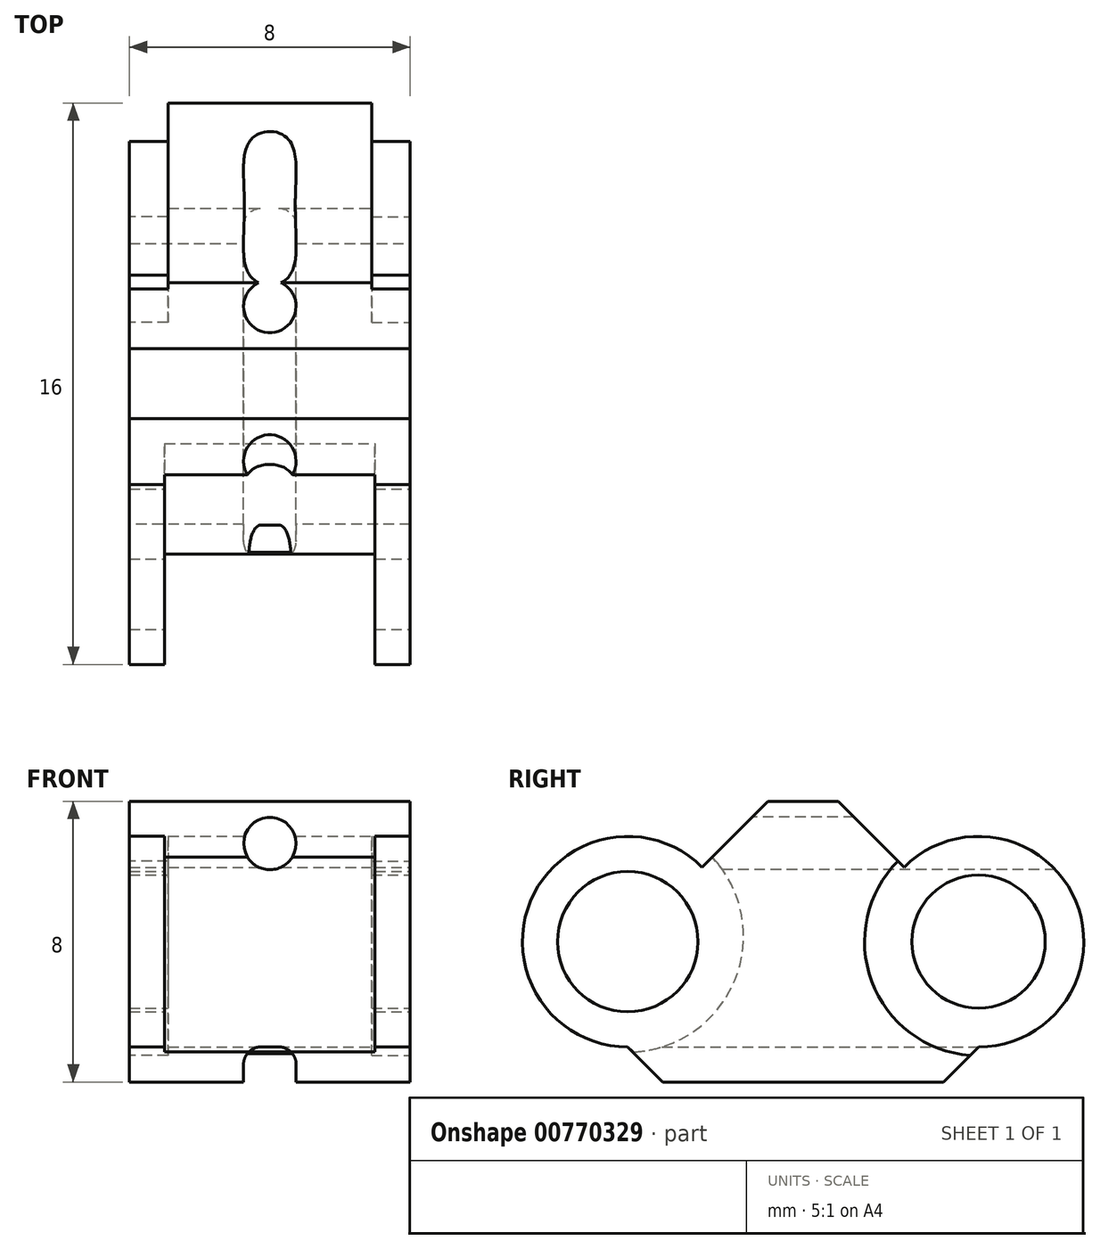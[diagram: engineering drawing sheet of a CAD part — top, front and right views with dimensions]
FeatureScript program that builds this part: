
annotation { "Feature Type Name" : "Feature", "Feature Type Description" : "" }
export const myFeature = defineFeature(function(context is Context, id is Id, definition is map)
    precondition{}
    {
        {
            var Q0;
            Q0=qCreatedBy(makeId("Top.planeOp"),FACE);
            var sketch = newSketch(context, id + "F0", { "sketchPlane" : qUnion([Q0])});
            skLineSegment(sketch, "E0.bottom", {"start": v(-4, 0) * mm, "end": v(4, 0) * mm});
            skLineSegment(sketch, "E0.top", {"start": v(-4, 10) * mm, "end": v(4, 10) * mm});
            skLineSegment(sketch, "E0.left", {"start": v(-4, 0) * mm, "end": v(-4, 10) * mm});
            skLineSegment(sketch, "E0.right", {"start": v(4, 0) * mm, "end": v(4, 10) * mm});
            skSolve(sketch);
        }
        {
            var Q0;
            Q0=makeQuery(id+"F0.imprint","IMPRINT",FACE,{"disambiguationData":[TD([[makeQuery(id+"F0.imprint","IMPRINT",EDGE,{"derivedFrom":sQuery(id+"F0.wireOp",EDGE,"E0.bottom")}),1.0]])]});
            extrude(context, id + "F1", {"entities" : qUnion([Q0]), "depth" : 8 * mm, "offsetDistance" : 25 * mm});
        }
        {
            var Q0;
            Q0=makeQuery(id+"F1.opExtrude","CAP_EDGE",EDGE,{"disambiguationData":[OSD([sQuery(id+"F0.wireOp",EDGE,"E0.bottom")])],"isStart":false});
            var Q1;
            Q1=makeQuery(id+"F1.opExtrude","CAP_EDGE",EDGE,{"disambiguationData":[OSD([sQuery(id+"F0.wireOp",EDGE,"E0.top")])],"isStart":false});
            chamfer(context, id + "F2", {"entities" : qUnion([Q0, Q1]), "width" : 4 * mm, "tangentPropagation" : true});
        }
        {
            var Q0;
            Q0=qCreatedBy(makeId("Right.planeOp"),FACE);
            var sketch = newSketch(context, id + "F3", { "sketchPlane" : qUnion([Q0])});
            skLineSegment(sketch, "E1.0.0", {"start": v(10, 0) * mm, "end": v(10, 4) * mm});
            skLineSegment(sketch, "E1.0.1", {"start": v(10, 4) * mm, "end": v(6, 8) * mm});
            skLineSegment(sketch, "E1.0.2", {"start": v(6, 8) * mm, "end": v(4, 8) * mm});
            skLineSegment(sketch, "E1.0.3", {"start": v(4, 8) * mm, "end": v(0, 4) * mm});
            skLineSegment(sketch, "E1.0.4", {"start": v(0, 4) * mm, "end": v(0, 0) * mm});
            skLineSegment(sketch, "E1.0.5", {"start": v(0, 0) * mm, "end": v(10, 0) * mm});
            skCircle(sketch, "E2", {"center": v(0, 4) * mm, "radius": 3 * mm});
            skCircle(sketch, "E3", {"center": v(10, 4) * mm, "radius": 3 * mm});
            skSolve(sketch);
        }
        {
            var Q0;
            {var subQ0=sQuery(id+"F3.wireOp",EDGE,"E1.0.4");var subQ1=sQuery(id+"F3.wireOp",EDGE,"E1.0.3");var subQ2=makeQuery(id+"F3.imprint","INTERSECT",VERTEX,{"derivedFrom":[subQ1,subQ0]});Q0=makeQuery(id+"F3.imprint","IMPRINT",FACE,{"disambiguationData":[TD([[makeQuery(id+"F3.imprint","IMPRINT",EDGE,{"disambiguationData":[TD([[subQ2,1.0]])],"derivedFrom":subQ1}),-1.0]])]});}
            extrude(context, id + "F4", {"entities" : qUnion([Q0]), "operationType" : NewBodyOperationType.ADD, "endBound" : BoundingType.SYMMETRIC, "oppositeDirection" : true, "depth" : 8 * mm, "offsetDistance" : 25 * mm});
        }
        {
            var Q0;
            {var subQ0=sQuery(id+"F3.wireOp",EDGE,"E1.0.1");var subQ1=sQuery(id+"F3.wireOp",EDGE,"E1.0.0");var subQ2=makeQuery(id+"F3.imprint","INTERSECT",VERTEX,{"derivedFrom":[subQ1,subQ0]});Q0=makeQuery(id+"F3.imprint","IMPRINT",FACE,{"disambiguationData":[TD([[makeQuery(id+"F3.imprint","IMPRINT",EDGE,{"disambiguationData":[TD([[subQ2,1.0]])],"derivedFrom":subQ1}),-1.0]])]});}
            extrude(context, id + "F5", {"entities" : qUnion([Q0]), "operationType" : NewBodyOperationType.ADD, "endBound" : BoundingType.SYMMETRIC, "oppositeDirection" : true, "depth" : 6 * mm, "offsetDistance" : 25 * mm});
        }
        {
            var Q0;
            Q0=qCreatedBy(makeId("Right.planeOp"),FACE);
            var sketch = newSketch(context, id + "F6", { "sketchPlane" : qUnion([Q0])});
            skCircle(sketch, "E4", {"center": v(0, 4.15) * mm, "radius": 3.3 * mm});
            skSolve(sketch);
        }
        {
            var Q0;
            Q0=makeQuery(id+"F6.imprint","IMPRINT",FACE,{"disambiguationData":[TD([[makeQuery(id+"F6.imprint","IMPRINT",EDGE,{"derivedFrom":sQuery(id+"F6.wireOp",EDGE,"E4")}),1.0]])]});
            extrude(context, id + "F7", {"entities" : qUnion([Q0]), "operationType" : NewBodyOperationType.REMOVE, "endBound" : BoundingType.SYMMETRIC, "oppositeDirection" : true, "depth" : 6 * mm, "offsetDistance" : 25 * mm});
        }
        {
            var Q0;
            Q0=makeQuery(id+"F4.boolean.opBoolean","MERGE",FACE,{"derivedFrom":[makeQuery(id+"F1.opExtrude","SWEPT_FACE",FACE,{"disambiguationData":[OSD([sQuery(id+"F0.wireOp",EDGE,"E0.left")])]}),makeQuery(id+"F4.opExtrude","CAP_FACE",FACE,{"disambiguationData":[OSD([sQuery(id+"F3.wireOp",EDGE,"E1.0.3"),sQuery(id+"F3.wireOp",EDGE,"E1.0.4"),sQuery(id+"F3.wireOp",EDGE,"E2")])],"isStart":false})]});
            var sketch = newSketch(context, id + "F8", { "sketchPlane" : qUnion([Q0])});
            skCircle(sketch, "E5", {"center": v(-10, 4) * mm, "radius": 3.25 * mm});
            skSolve(sketch);
        }
        {
            var Q0;
            {var subQ0=sQuery(id+"F8.wireOp",EDGE,"E5");var subQ1=sQuery(id+"F0.wireOp",EDGE,"E0.left");var subQ2=sQuery(id+"F0.wireOp",EDGE,"E0.top");var subQ3=makeQuery(id+"F1.opExtrude","SWEPT_EDGE",EDGE,{"disambiguationData":[OSD([subQ2,subQ1])]});var subQ4=makeQuery(id+"F8.imprint","INTERSECT",VERTEX,{"derivedFrom":[subQ3,subQ0]});Q0=makeQuery(id+"F8.imprint","IMPRINT",FACE,{"disambiguationData":[TD([[makeQuery(id+"F8.imprint","IMPRINT",EDGE,{"disambiguationData":[TD([[subQ4,1.0]])],"derivedFrom":subQ0}),1.0]])]});}
            var Q1;
            {var subQ0=sQuery(id+"F8.wireOp",EDGE,"E5");var subQ1=sQuery(id+"F0.wireOp",EDGE,"E0.left");var subQ2=sQuery(id+"F0.wireOp",EDGE,"E0.top");var subQ3=makeQuery(id+"F1.opExtrude","SWEPT_EDGE",EDGE,{"disambiguationData":[OSD([subQ2,subQ1])]});var subQ4=makeQuery(id+"F8.imprint","INTERSECT",VERTEX,{"derivedFrom":[subQ3,subQ0]});Q1=makeQuery(id+"F8.imprint","IMPRINT",FACE,{"disambiguationData":[TD([[makeQuery(id+"F8.imprint","IMPRINT",EDGE,{"disambiguationData":[TD([[subQ4,-1.0]])],"derivedFrom":subQ0}),1.0]])]});}
            extrude(context, id + "F9", {"entities" : qUnion([Q0, Q1]), "operationType" : NewBodyOperationType.REMOVE, "oppositeDirection" : true, "depth" : 1.1 * mm, "offsetDistance" : 25 * mm});
        }
        {
            var Q0;
            Q0=makeQuery(id+"F1.opExtrude","SWEPT_BODY",BODY,{"disambiguationData":[OSD([sQuery(id+"F0.wireOp",EDGE,"E0.bottom"),sQuery(id+"F0.wireOp",EDGE,"E0.top"),sQuery(id+"F0.wireOp",EDGE,"E0.left"),sQuery(id+"F0.wireOp",EDGE,"E0.right")])]});
            var Q1;
            Q1=qCreatedBy(makeId("Right.planeOp"),FACE);
            mirror(context, id + "F10", {"operationType" : NewBodyOperationType.INTERSECT, "entities" : qUnion([Q0]), "mirrorPlane" : qUnion([Q1])});
        }
        {
            var Q0;
            Q0=qCreatedBy(makeId("Right.planeOp"),FACE);
            var sketch = newSketch(context, id + "F11", { "sketchPlane" : qUnion([Q0])});
            skArc(sketch, "E6.0", {"start": v(10, 1) * mm, "mid": v(12.77, 5.15) * mm, "end": v(7.88, 6.12) * mm});
            skCircle(sketch, "E7", {"center": v(10, 4) * mm, "radius": 1.9 * mm});
            skSolve(sketch);
        }
        {
            var Q0;
            Q0 = qSketchRegion(id + "F11", true);
            extrude(context, id + "F12", {"entities" : qUnion([Q0]), "operationType" : NewBodyOperationType.ADD, "endBound" : BoundingType.SYMMETRIC, "oppositeDirection" : true, "depth" : 8 * mm, "offsetDistance" : 25 * mm});
        }
        {
            var Q0;
            Q0=qCreatedBy(makeId("Right.planeOp"),FACE);
            var sketch = newSketch(context, id + "F13", { "sketchPlane" : qUnion([Q0])});
            skCircle(sketch, "E8.0", {"center": v(0, 4) * mm, "radius": 3 * mm});
            skCircle(sketch, "E9", {"center": v(0, 4) * mm, "radius": 2 * mm});
            skSolve(sketch);
        }
        {
            var Q0;
            Q0=makeQuery(id+"F13.imprint","IMPRINT",FACE,{"disambiguationData":[TD([[makeQuery(id+"F13.imprint","IMPRINT",EDGE,{"derivedFrom":sQuery(id+"F13.wireOp",EDGE,"E9")}),1.0]])]});
            extrude(context, id + "F14", {"entities" : qUnion([Q0]), "operationType" : NewBodyOperationType.REMOVE, "endBound" : BoundingType.SYMMETRIC, "oppositeDirection" : true, "depth" : 25 * mm, "offsetDistance" : 25 * mm});
        }
        {
            var Q0;
            Q0=makeQuery(id+"F1.opExtrude","CAP_EDGE",EDGE,{"disambiguationData":[OSD([sQuery(id+"F0.wireOp",EDGE,"E0.top")])],"isStart":true});
            var Q1;
            Q1=makeQuery(id+"F1.opExtrude","CAP_EDGE",EDGE,{"disambiguationData":[OSD([sQuery(id+"F0.wireOp",EDGE,"E0.bottom")])],"isStart":true});
            chamfer(context, id + "F15", {"entities" : qUnion([Q0, Q1]), "width" : 1 * mm, "tangentPropagation" : true});
        }
        {
            var Q0;
            Q0=makeQuery(id+"F1.opExtrude","CAP_FACE",FACE,{"disambiguationData":[OSD([sQuery(id+"F0.wireOp",EDGE,"E0.bottom"),sQuery(id+"F0.wireOp",EDGE,"E0.top"),sQuery(id+"F0.wireOp",EDGE,"E0.left"),sQuery(id+"F0.wireOp",EDGE,"E0.right")])],"isStart":true});
            var sketch = newSketch(context, id + "F16", { "sketchPlane" : qUnion([Q0])});
            skLineSegment(sketch, "E10.bottom", {"start": v(-0.75, -0.2) * mm, "end": v(0.75, -0.2) * mm});
            skLineSegment(sketch, "E10.top", {"start": v(-0.75, -10.07) * mm, "end": v(0.75, -10.07) * mm});
            skLineSegment(sketch, "E10.left", {"start": v(-0.75, -0.2) * mm, "end": v(-0.75, -10.07) * mm});
            skLineSegment(sketch, "E10.right", {"start": v(0.75, -0.2) * mm, "end": v(0.75, -10.07) * mm});
            skSolve(sketch);
        }
        {
            var Q0;
            {var subQ0=sQuery(id+"F16.wireOp",EDGE,"E10.top");Q0=makeQuery(id+"F16.imprint","IMPRINT",FACE,{"disambiguationData":[TD([[makeQuery(id+"F16.imprint","IMPRINT",EDGE,{"derivedFrom":subQ0}),1.0]])]});}
            var Q1;
            {var subQ0=sQuery(id+"F16.wireOp",EDGE,"E10.left");var subQ1=sQuery(id+"F0.wireOp",EDGE,"E0.top");var subQ2=sQuery(id+"F0.wireOp",EDGE,"E0.bottom");var subQ3=makeQuery(id+"F1.opExtrude","CAP_FACE",FACE,{"disambiguationData":[OSD([subQ2,subQ1,sQuery(id+"F0.wireOp",EDGE,"E0.left"),sQuery(id+"F0.wireOp",EDGE,"E0.right")])],"isStart":true});var subQ4=makeQuery(id+"F15.opChamfer","BLEND_EDGE",EDGE,{"blendedFrom":[makeQuery(id+"F1.opExtrude","CAP_EDGE",EDGE,{"disambiguationData":[OSD([subQ2])],"isStart":true}),subQ3],"blendedInto":[subQ3]});var subQ5=makeQuery(id+"F16.imprint","INTERSECT",VERTEX,{"derivedFrom":[subQ4,subQ0]});Q1=makeQuery(id+"F16.imprint","IMPRINT",FACE,{"disambiguationData":[TD([[makeQuery(id+"F16.imprint","IMPRINT",EDGE,{"disambiguationData":[TD([[subQ5,-1.0]])],"derivedFrom":subQ0}),1.0]])]});}
            var Q2;
            {var subQ0=sQuery(id+"F16.wireOp",EDGE,"E10.bottom");Q2=makeQuery(id+"F16.imprint","IMPRINT",FACE,{"disambiguationData":[TD([[makeQuery(id+"F16.imprint","IMPRINT",EDGE,{"derivedFrom":subQ0}),-1.0]])]});}
            extrude(context, id + "F17", {"entities" : qUnion([Q0, Q1, Q2]), "operationType" : NewBodyOperationType.REMOVE, "oppositeDirection" : true, "depth" : 1 * mm, "offsetDistance" : 25 * mm});
        }
        {
            var Q0;
            Q0=makeQuery(id+"F17.boolean.opBoolean","COPY",EDGE,{"derivedFrom":makeQuery(id+"F17.opExtrude","CAP_EDGE",EDGE,{"disambiguationData":[OSD([sQuery(id+"F16.wireOp",EDGE,"E10.left")])],"isStart":false})});
            var Q1;
            Q1=makeQuery(id+"F17.boolean.opBoolean","COPY",EDGE,{"derivedFrom":makeQuery(id+"F17.opExtrude","CAP_EDGE",EDGE,{"disambiguationData":[OSD([sQuery(id+"F16.wireOp",EDGE,"E10.right")])],"isStart":false})});
            fillet(context, id + "F18", {"entities" : qUnion([Q0, Q1]), "radius" : 0.5 * mm, "tangentPropagation" : true, "allowEdgeOverflow" : false});
        }
        {
            var Q0;
            Q0=qCreatedBy(makeId("Front.planeOp"),FACE);
            var sketch = newSketch(context, id + "F19", { "sketchPlane" : qUnion([Q0])});
            skCircle(sketch, "E11", {"center": v(0, 6.8) * mm, "radius": 0.75 * mm});
            skLineSegment(sketch, "E12.0", {"start": v(-4, 8) * mm, "end": v(4, 8) * mm});
            skSolve(sketch);
        }
        {
            var Q0;
            Q0=makeQuery(id+"F19.imprint","IMPRINT",FACE,{"disambiguationData":[TD([[makeQuery(id+"F19.imprint","IMPRINT",EDGE,{"derivedFrom":sQuery(id+"F19.wireOp",EDGE,"E11")}),1.0]])]});
            extrude(context, id + "F20", {"entities" : qUnion([Q0]), "operationType" : NewBodyOperationType.REMOVE, "oppositeDirection" : true, "depth" : 25 * mm, "offsetDistance" : 25 * mm});
        }
    });
